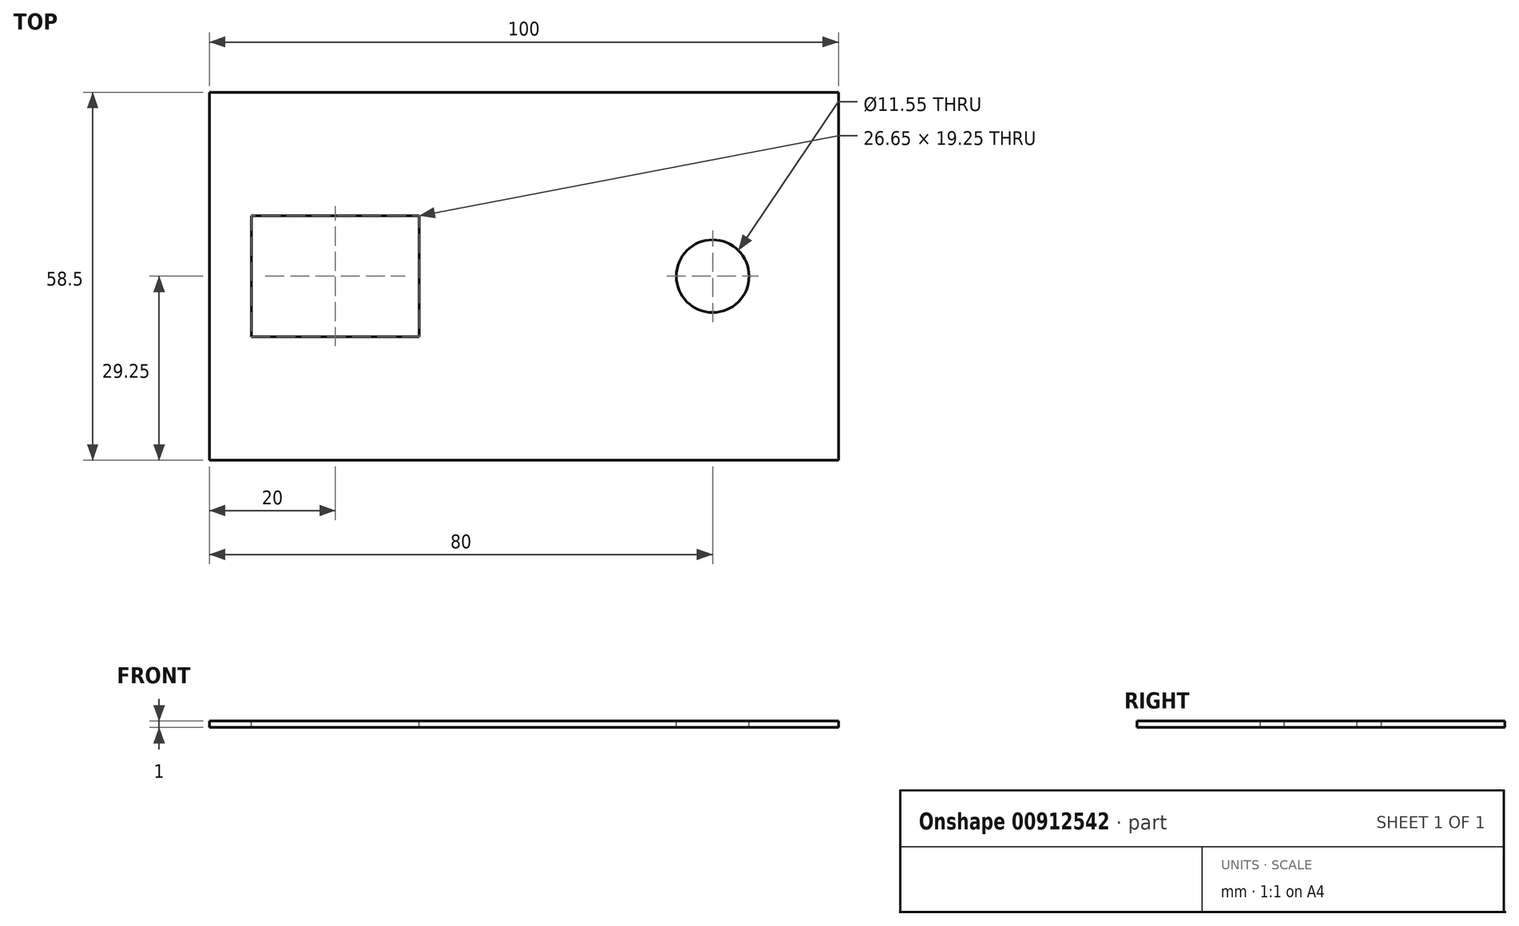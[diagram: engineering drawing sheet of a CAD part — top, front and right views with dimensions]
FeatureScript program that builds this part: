
annotation { "Feature Type Name" : "Feature", "Feature Type Description" : "" }
export const myFeature = defineFeature(function(context is Context, id is Id, definition is map)
    precondition{}
    {
        {
            var Q0;
            Q0=qCreatedBy(makeId("Top.planeOp"),FACE);
            var sketch = newSketch(context, id + "F0", { "sketchPlane" : qUnion([Q0])});
            skLineSegment(sketch, "E0.bottom", {"start": v(50, 29.25) * mm, "end": v(-50, 29.25) * mm});
            skLineSegment(sketch, "E0.top", {"start": v(50, -29.25) * mm, "end": v(-50, -29.25) * mm});
            skLineSegment(sketch, "E0.left", {"start": v(50, 29.25) * mm, "end": v(50, -29.25) * mm});
            skLineSegment(sketch, "E0.right", {"start": v(-50, 29.25) * mm, "end": v(-50, -29.25) * mm});
            skPoint(sketch, "E0.middle", {"position": v(0, 0) * mm});
            skSolve(sketch);
        }
        {
            var Q0;
            Q0=makeQuery(id+"F0.imprint","IMPRINT",FACE,{"disambiguationData":[TD([[makeQuery(id+"F0.imprint","IMPRINT",EDGE,{"derivedFrom":sQuery(id+"F0.wireOp",EDGE,"E0.bottom")}),1.0]])]});
            extrude(context, id + "F1", {"entities" : qUnion([Q0]), "depth" : 1 * mm, "offsetDistance" : 25 * mm});
        }
        {
            var Q0;
            Q0=makeQuery(id+"F1.opExtrude","CAP_FACE",FACE,{"disambiguationData":[OSD([sQuery(id+"F0.wireOp",EDGE,"E0.bottom"),sQuery(id+"F0.wireOp",EDGE,"E0.top"),sQuery(id+"F0.wireOp",EDGE,"E0.left"),sQuery(id+"F0.wireOp",EDGE,"E0.right")])],"isStart":false});
            var sketch = newSketch(context, id + "F2", { "sketchPlane" : qUnion([Q0])});
            skLineSegment(sketch, "E1.bottom", {"start": v(-16.68, 9.63) * mm, "end": v(-43.33, 9.63) * mm});
            skLineSegment(sketch, "E1.top", {"start": v(-16.68, -9.62) * mm, "end": v(-43.33, -9.62) * mm});
            skLineSegment(sketch, "E1.left", {"start": v(-16.68, 9.63) * mm, "end": v(-16.68, -9.62) * mm});
            skLineSegment(sketch, "E1.right", {"start": v(-43.33, 9.63) * mm, "end": v(-43.33, -9.62) * mm});
            skPoint(sketch, "E1.middle", {"position": v(-30, 0) * mm});
            skLineSegment(sketch, "E2", {"start": v(0, 0) * mm, "end": v(-50, 0) * mm, "construction": true});
            skSolve(sketch);
        }
        {
            var Q0;
            Q0=makeQuery(id+"F1.opExtrude","CAP_FACE",FACE,{"disambiguationData":[OSD([sQuery(id+"F0.wireOp",EDGE,"E0.bottom"),sQuery(id+"F0.wireOp",EDGE,"E0.top"),sQuery(id+"F0.wireOp",EDGE,"E0.left"),sQuery(id+"F0.wireOp",EDGE,"E0.right")])],"isStart":false});
            var sketch = newSketch(context, id + "F3", { "sketchPlane" : qUnion([Q0])});
            skCircle(sketch, "E3", {"center": v(30, 0) * mm, "radius": 5.77 * mm});
            skLineSegment(sketch, "E4", {"start": v(0, 0) * mm, "end": v(50, 0) * mm, "construction": true});
            skSolve(sketch);
        }
        {
            var Q0;
            Q0=makeQuery(id+"F2.imprint","IMPRINT",FACE,{"disambiguationData":[TD([[makeQuery(id+"F2.imprint","IMPRINT",EDGE,{"derivedFrom":sQuery(id+"F2.wireOp",EDGE,"E1.bottom")}),1.0]])]});
            var Q1;
            Q1 = qSketchRegion(id + "F3", true);
            extrude(context, id + "F4", {"entities" : qUnion([Q0, Q1]), "operationType" : NewBodyOperationType.REMOVE, "oppositeDirection" : true, "depth" : 25 * mm, "offsetDistance" : 25 * mm});
        }
    });
